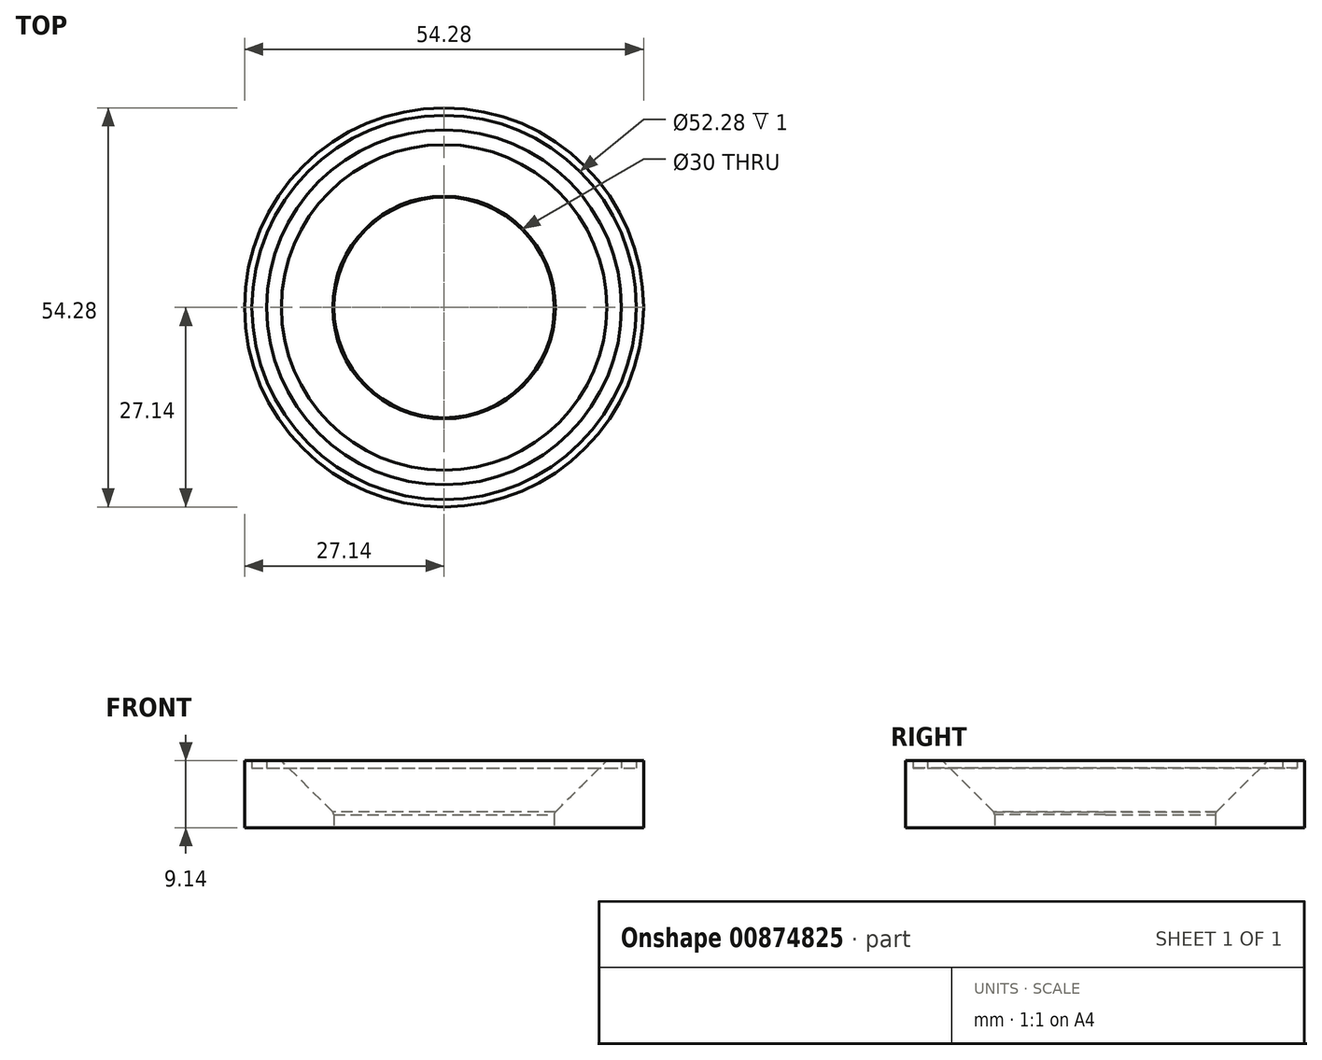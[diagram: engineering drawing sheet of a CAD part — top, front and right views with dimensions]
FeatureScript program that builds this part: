
annotation { "Feature Type Name" : "Feature", "Feature Type Description" : "" }
export const myFeature = defineFeature(function(context is Context, id is Id, definition is map)
    precondition{}
    {
        {
            var Q0;
            Q0=qCreatedBy(makeId("Front.planeOp"),FACE);
            var sketch = newSketch(context, id + "F0", { "sketchPlane" : qUnion([Q0])});
            skPoint(sketch, "E0.endSnap0", {"position": v(-14.28, 7.14) * mm});
            skLineSegment(sketch, "E1", {"start": v(0, 0) * mm, "end": v(-7.14, 7.14) * mm});
            skPoint(sketch, "E2.endSnap0", {"position": v(0, 7.14) * mm});
            skPoint(sketch, "E3.orphan", {"position": v(-14.28, 14.28) * mm});
            skPoint(sketch, "E4.right.start.orphan", {"position": v(-14.28, 0) * mm});
            skPoint(sketch, "E4.bottom.end.orphan", {"position": v(-7.14, 0) * mm});
            skLineSegment(sketch, "E5", {"start": v(0, 0) * mm, "end": v(0, -2) * mm});
            skLineSegment(sketch, "E6", {"start": v(-7.14, 7.14) * mm, "end": v(-12.14, 7.14) * mm});
            skLineSegment(sketch, "E7", {"start": v(0, -2) * mm, "end": v(-12.14, -2) * mm});
            skLineSegment(sketch, "E8", {"start": v(-12.14, -2) * mm, "end": v(-12.14, 7.14) * mm});
            skPoint(sketch, "E9.end.orphan", {"position": v(15, 7.14) * mm});
            skPoint(sketch, "E9.start.orphan", {"position": v(7.14, 7.14) * mm});
            skPoint(sketch, "E10.end.orphan", {"position": v(15, -2) * mm});
            skPoint(sketch, "E11.end.orphan", {"position": v(0, 14.28) * mm});
            skPoint(sketch, "E11.start.orphan", {"position": v(-9.64, 14.28) * mm});
            skLineSegment(sketch, "E12", {"start": v(15, -2) * mm, "end": v(15, 7.14) * mm});
            skLineSegment(sketch, "E13", {"start": v(-12.14, 7.14) * mm, "end": v(-11.14, 7.14) * mm});
            skLineSegment(sketch, "E14", {"start": v(-11.14, 7.14) * mm, "end": v(-9.14, 7.14) * mm});
            skLineSegment(sketch, "E15", {"start": v(-9.14, 7.14) * mm, "end": v(-7.14, 7.14) * mm});
            skLineSegment(sketch, "E16", {"start": v(-11.14, 7.14) * mm, "end": v(-11.14, 6.14) * mm});
            skLineSegment(sketch, "E17", {"start": v(-11.14, 6.14) * mm, "end": v(-9.14, 6.14) * mm});
            skLineSegment(sketch, "E18", {"start": v(-9.14, 6.14) * mm, "end": v(-9.14, 7.14) * mm});
            skSolve(sketch);
        }
        {
            var Q0;
            {var subQ3=sQuery(id+"F0.wireOp",EDGE,"E1");Q0=makeQuery(id+"F0.imprint","IMPRINT",FACE,{"disambiguationData":[TD([[makeQuery(id+"F0.imprint","IMPRINT",EDGE,{"derivedFrom":subQ3}),1.0]])]});}
            var Q1;
            Q1=sQuery(id+"F0.wireOp",EDGE,"E12");
            revolve(context, id + "F1", {"surfaceOperationType" : NewSurfaceOperationType.NEW, "entities" : qUnion([Q0]), "axis" : qUnion([Q1]), "revolveType" : RevolveType.FULL});
        }
        {
            var Q0;
            Q0=makeQuery(id+"F1.opRevolve","SWEPT_EDGE",EDGE,{"disambiguationData":[OSD([sQuery(id+"F0.wireOp",EDGE,"E1"),sQuery(id+"F0.wireOp",EDGE,"E5")])]});
            chamfer(context, id + "F2", {"entities" : qUnion([Q0]), "width" : 0.5 * mm, "tangentPropagation" : true});
        }
    });
